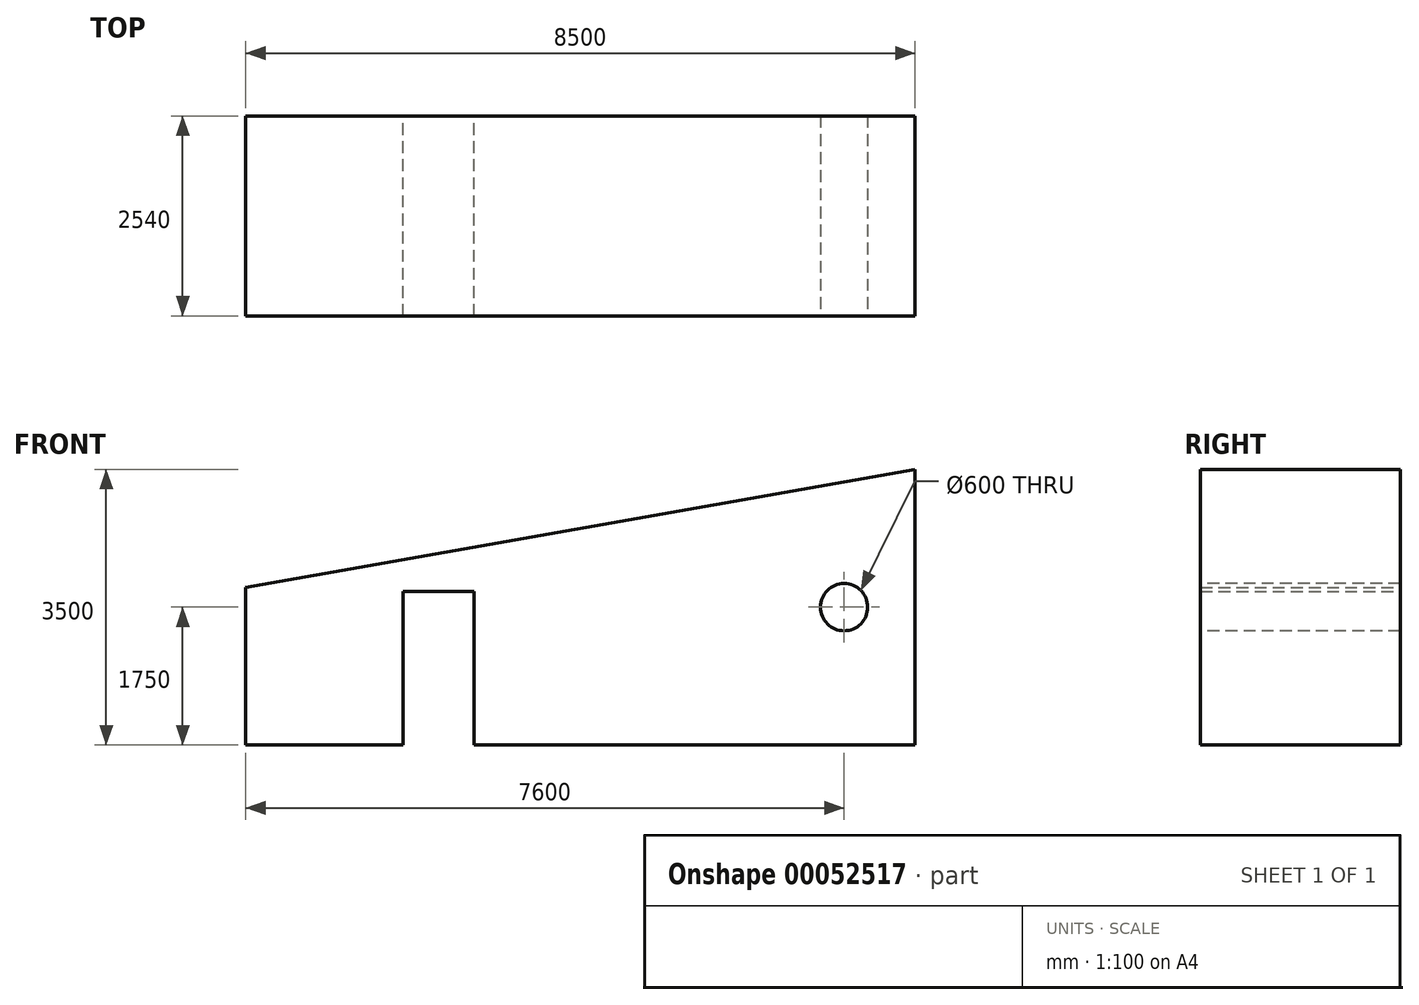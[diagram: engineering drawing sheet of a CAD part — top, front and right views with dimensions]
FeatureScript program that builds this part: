
annotation { "Feature Type Name" : "Feature", "Feature Type Description" : "" }
export const myFeature = defineFeature(function(context is Context, id is Id, definition is map)
    precondition{}
    {
        {
            var Q0;
            Q0=qCreatedBy(makeId("Front.planeOp"),FACE);
            var sketch = newSketch(context, id + "F0", { "sketchPlane" : qUnion([Q0])});
            skLineSegment(sketch, "E0.bottom", {"start": v(0, 0) * mm, "end": v(-8500, 0) * mm});
            skLineSegment(sketch, "E0.top", {"start": v(0, 3500) * mm, "end": v(-8500, 2000) * mm});
            skLineSegment(sketch, "E0.left", {"start": v(0, 0) * mm, "end": v(0, 3500) * mm});
            skLineSegment(sketch, "E0.right", {"start": v(-8500, 0) * mm, "end": v(-8500, 2000) * mm});
            skSolve(sketch);
        }
        {
            var Q0;
            Q0=makeQuery(id+"F0.imprint","IMPRINT",FACE,{"disambiguationData":[TD([[makeQuery(id+"F0.imprint","IMPRINT",EDGE,{"derivedFrom":sQuery(id+"F0.wireOp",EDGE,"E0.bottom")}),-1.0]])]});
            var sketch = newSketch(context, id + "F1", { "sketchPlane" : qUnion([Q0])});
            skLineSegment(sketch, "E1.bottom", {"start": v(-5600, 1950) * mm, "end": v(-6500, 1950) * mm});
            skLineSegment(sketch, "E1.top", {"start": v(-5600, 0) * mm, "end": v(-6500, 0) * mm});
            skLineSegment(sketch, "E1.left", {"start": v(-5600, 1950) * mm, "end": v(-5600, 0) * mm});
            skLineSegment(sketch, "E1.right", {"start": v(-6500, 1950) * mm, "end": v(-6500, 0) * mm});
            skSolve(sketch);
        }
        {
            var Q0;
            Q0 = qSketchRegion(id + "F0", true);
            extrude(context, id + "F2", {"entities" : qUnion([Q0]), "depth" : 2540 * mm});
        }
        {
            var Q0;
            Q0 = qSketchRegion(id + "F1", true);
            extrude(context, id + "F3", {"entities" : qUnion([Q0]), "operationType" : NewBodyOperationType.REMOVE, "endBound" : BoundingType.THROUGH_ALL, "depth" : 25.4 * mm});
        }
        {
            var Q0;
            Q0=makeQuery(id+"F2.opExtrude","CAP_FACE",FACE,{"disambiguationData":[OSD([sQuery(id+"F0.wireOp",EDGE,"E0.bottom"),sQuery(id+"F0.wireOp",EDGE,"E0.top"),sQuery(id+"F0.wireOp",EDGE,"E0.left"),sQuery(id+"F0.wireOp",EDGE,"E0.right")])],"isStart":false});
            var sketch = newSketch(context, id + "F4", { "sketchPlane" : qUnion([Q0])});
            skCircle(sketch, "E2", {"center": v(-900, 1750) * mm, "radius": 300 * mm});
            skSolve(sketch);
        }
        {
            var Q0;
            Q0 = qSketchRegion(id + "F4", true);
            extrude(context, id + "F5", {"entities" : qUnion([Q0]), "operationType" : NewBodyOperationType.REMOVE, "endBound" : BoundingType.THROUGH_ALL, "oppositeDirection" : true, "depth" : 25.4 * mm});
        }
    });
